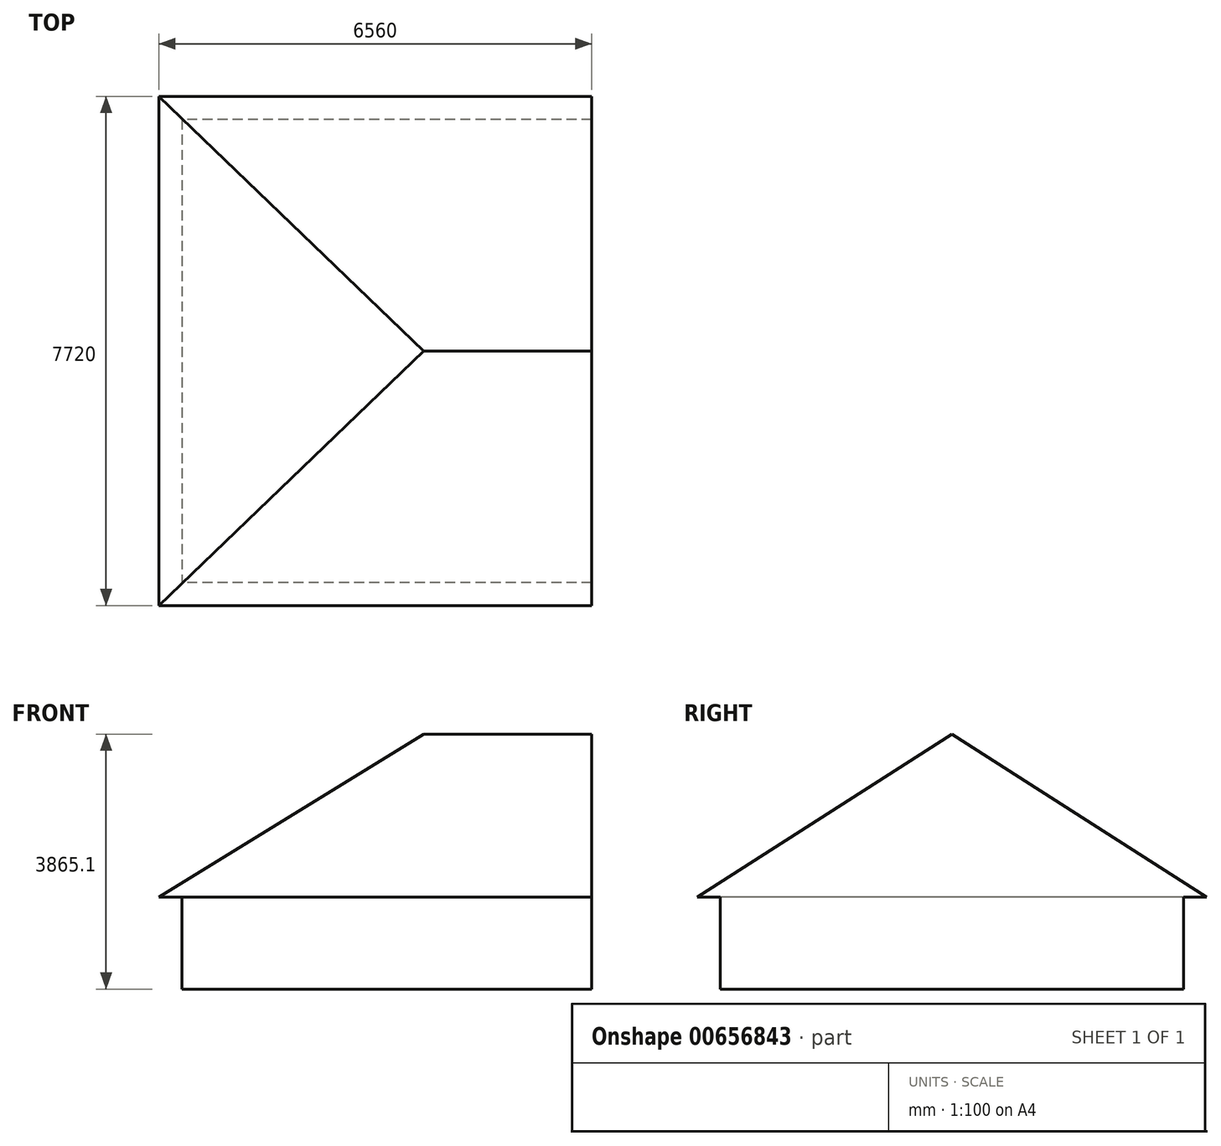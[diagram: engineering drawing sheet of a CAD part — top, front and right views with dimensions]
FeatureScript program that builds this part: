
annotation { "Feature Type Name" : "Feature", "Feature Type Description" : "" }
export const myFeature = defineFeature(function(context is Context, id is Id, definition is map)
    precondition{}
    {
        {
            var Q0;
            Q0=qCreatedBy(makeId("Right.planeOp"),FACE);
            var sketch = newSketch(context, id + "F0", { "sketchPlane" : qUnion([Q0])});
            skLineSegment(sketch, "E0", {"start": v(0, 0) * mm, "end": v(-1625, 0) * mm, "construction": true});
            skLineSegment(sketch, "E1", {"start": v(0, 0) * mm, "end": v(1625, 0) * mm, "construction": true});
            skLineSegment(sketch, "E2", {"start": v(-1625, 0) * mm, "end": v(0, 1040) * mm});
            skLineSegment(sketch, "E3", {"start": v(0, 0) * mm, "end": v(0, 1040) * mm, "construction": true});
            skLineSegment(sketch, "E4", {"start": v(0, 1040) * mm, "end": v(1625, 0) * mm});
            skLineSegment(sketch, "E5", {"start": v(-1625, 0) * mm, "end": v(-3860, -1430.4) * mm});
            skLineSegment(sketch, "E6", {"start": v(-3860, -1430.4) * mm, "end": v(-3510, -1430.4) * mm});
            skLineSegment(sketch, "E7", {"start": v(1625, 0) * mm, "end": v(3860, -1430.4) * mm});
            skLineSegment(sketch, "E8", {"start": v(3860, -1430.4) * mm, "end": v(3510, -1430.4) * mm});
            skLineSegment(sketch, "E9.bottom", {"start": v(-3510, -1323.2) * mm, "end": v(3510, -1323.2) * mm, "construction": true});
            skLineSegment(sketch, "E9.top", {"start": v(-3510, -2825.1) * mm, "end": v(3510, -2825.1) * mm});
            skLineSegment(sketch, "E9.left", {"start": v(-3510, -1323.2) * mm, "end": v(-3510, -2825.1) * mm});
            skLineSegment(sketch, "E9.right", {"start": v(3510, -1323.2) * mm, "end": v(3510, -2825.1) * mm});
            skLineSegment(sketch, "E10.bottom", {"start": v(-1497.22, -2825.1) * mm, "end": v(-860, -2825.1) * mm});
            skLineSegment(sketch, "E10.top", {"start": v(-1497.22, -1974.63) * mm, "end": v(-860, -1974.63) * mm, "construction": true});
            skLineSegment(sketch, "E10.left", {"start": v(-1497.22, -2825.1) * mm, "end": v(-1497.22, -1974.63) * mm, "construction": true});
            skLineSegment(sketch, "E10.right", {"start": v(-860, -2825.1) * mm, "end": v(-860, -1974.63) * mm, "construction": true});
            skLineSegment(sketch, "E11.bottom", {"start": v(2955, -1497.17) * mm, "end": v(3030, -1497.17) * mm, "construction": true});
            skLineSegment(sketch, "E11.top", {"start": v(2955, -2825.1) * mm, "end": v(3030, -2825.1) * mm});
            skLineSegment(sketch, "E11.left", {"start": v(2955, -1497.17) * mm, "end": v(2955, -2825.1) * mm, "construction": true});
            skLineSegment(sketch, "E11.right", {"start": v(3030, -1497.17) * mm, "end": v(3030, -2825.1) * mm, "construction": true});
            skSolve(sketch);
        }
        {
            var Q0;
            Q0 = qSketchRegion(id + "F0", true);
            extrude(context, id + "F1", {"entities" : qUnion([Q0]), "depth" : (2150 + 400) * mm, "offsetDistance" : 25 * mm, "hasSecondDirection" : true, "secondDirectionOppositeDirection" : true, "secondDirectionDepth" : 4870 * mm});
        }
        {
            var Q0;
            Q0=makeQuery(id+"F1.opExtrude","SWEPT_FACE",FACE,{"disambiguationData":[OSD([sQuery(id+"F0.wireOp",EDGE,"E9.left")])]});
            var sketch = newSketch(context, id + "F2", { "sketchPlane" : qUnion([Q0])});
            skLineSegment(sketch, "E12", {"start": v(-3660, -1430.4) * mm, "end": v(-3660, -2825.1) * mm});
            skLineSegment(sketch, "E13", {"start": v(-3660, -1430.4) * mm, "end": v(-4010, -1430.4) * mm});
            skLineSegment(sketch, "E14", {"start": v(-4010, -1430.4) * mm, "end": v(0, 1040) * mm});
            skLineSegment(sketch, "E15", {"start": v(0, 1040) * mm, "end": v(0, 1641.88) * mm});
            skLineSegment(sketch, "E16", {"start": v(0, 1641.88) * mm, "end": v(-5604.51, 1641.88) * mm});
            skLineSegment(sketch, "E17", {"start": v(-5604.51, 1641.88) * mm, "end": v(-5604.51, -4045.94) * mm});
            skLineSegment(sketch, "E18", {"start": v(-5604.51, -4045.94) * mm, "end": v(0, -4045.94) * mm});
            skLineSegment(sketch, "E19", {"start": v(0, -4045.94) * mm, "end": v(0, -2825.1) * mm});
            skLineSegment(sketch, "E20", {"start": v(0, -2825.1) * mm, "end": v(-3660, -2825.1) * mm});
            skSolve(sketch);
        }
        {
            var Q0;
            {var subQ4=sQuery(id+"F2.wireOp",EDGE,"E14");Q0=makeQuery(id+"F2.imprint","IMPRINT",FACE,{"disambiguationData":[TD([[makeQuery(id+"F2.imprint","IMPRINT",EDGE,{"derivedFrom":subQ4}),1.0]])]});}
            var Q1;
            {var subQ4=sQuery(id+"F2.wireOp",EDGE,"E12");Q1=makeQuery(id+"F2.imprint","IMPRINT",FACE,{"disambiguationData":[TD([[makeQuery(id+"F2.imprint","IMPRINT",EDGE,{"derivedFrom":subQ4}),-1.0]])]});}
            extrude(context, id + "F3", {"entities" : qUnion([Q0, Q1]), "operationType" : NewBodyOperationType.REMOVE, "endBound" : BoundingType.THROUGH_ALL, "oppositeDirection" : true, "depth" : 25 * mm, "offsetDistance" : 25 * mm, "hasSecondDirection" : true, "secondDirectionBound" : SecondDirectionBoundingType.THROUGH_ALL, "secondDirectionOppositeDirection" : false, "secondDirectionDepth" : 25 * mm});
        }
    });
